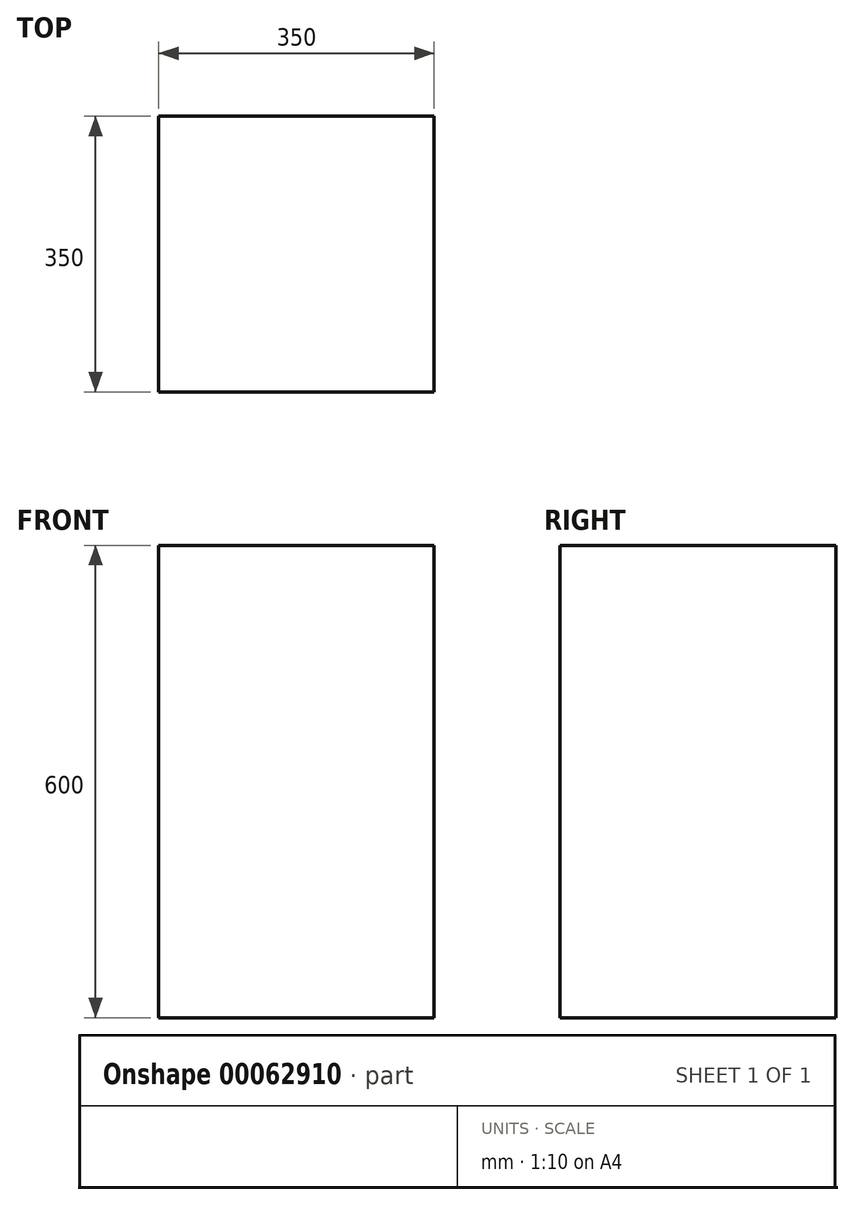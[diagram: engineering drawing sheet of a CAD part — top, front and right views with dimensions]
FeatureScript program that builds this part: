
annotation { "Feature Type Name" : "Feature", "Feature Type Description" : "" }
export const myFeature = defineFeature(function(context is Context, id is Id, definition is map)
    precondition{}
    {
        {
            var Q0;
            Q0=qCreatedBy(makeId("Top.planeOp"),FACE);
            var sketch = newSketch(context, id + "F0", { "sketchPlane" : qUnion([Q0])});
            skLineSegment(sketch, "E0.bottom", {"start": v(-179.75, -175) * mm, "end": v(170.25, -175) * mm});
            skLineSegment(sketch, "E0.top", {"start": v(-179.75, 175) * mm, "end": v(170.25, 175) * mm});
            skLineSegment(sketch, "E0.left", {"start": v(-179.75, -175) * mm, "end": v(-179.75, 175) * mm});
            skLineSegment(sketch, "E0.right", {"start": v(170.25, -175) * mm, "end": v(170.25, 175) * mm});
            skLineSegment(sketch, "E1", {"start": v(0, 175) * mm, "end": v(0, 0) * mm, "construction": true});
            skLineSegment(sketch, "E2", {"start": v(0, 0) * mm, "end": v(-179.75, 0) * mm, "construction": true});
            skSolve(sketch);
        }
        {
            var Q0;
            Q0 = qSketchRegion(id + "F0", true);
            extrude(context, id + "F1", {"entities" : qUnion([Q0]), "depth" : 600 * mm});
        }
    });
